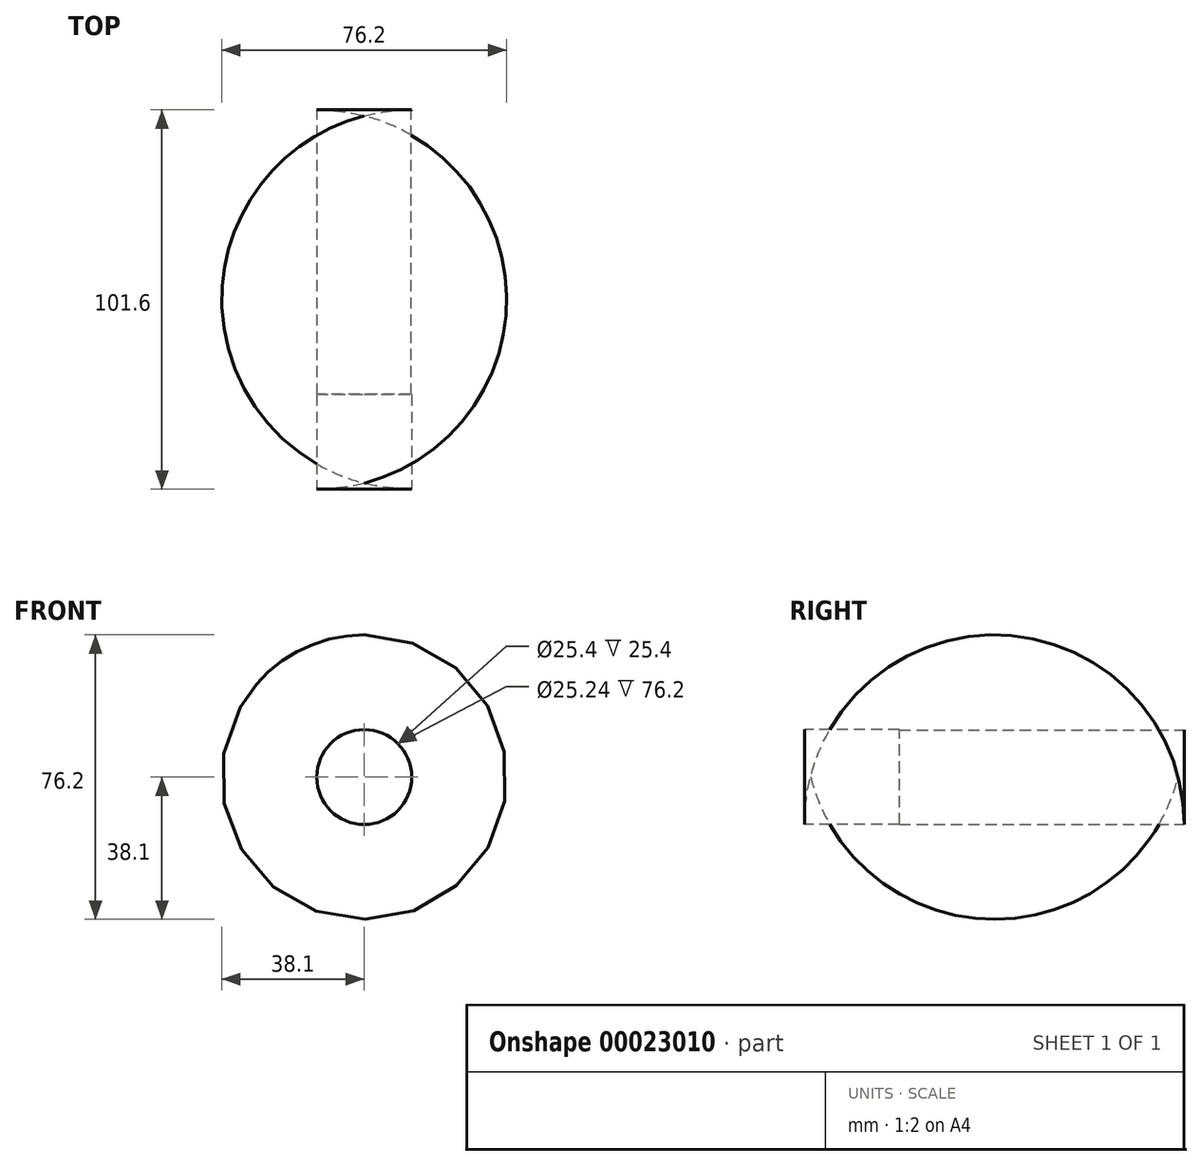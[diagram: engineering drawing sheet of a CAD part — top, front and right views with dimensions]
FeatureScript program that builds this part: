
annotation { "Feature Type Name" : "Feature", "Feature Type Description" : "" }
export const myFeature = defineFeature(function(context is Context, id is Id, definition is map)
    precondition{}
    {
        {
            var Q0;
            Q0=qCreatedBy(makeId("Front.planeOp"),FACE);
            var sketch = newSketch(context, id + "F0", { "sketchPlane" : qUnion([Q0])});
            skCircle(sketch, "E0", {"center": v(0, 0) * mm, "radius": 63.5 * mm});
            skSolve(sketch);
        }
        {
            var Q0;
            Q0=makeQuery(id+"F0.imprint","IMPRINT",FACE,{"disambiguationData":[TD([[makeQuery(id+"F0.imprint","IMPRINT",EDGE,{"derivedFrom":sQuery(id+"F0.wireOp",EDGE,"E0")}),1.0]])]});
            extrude(context, id + "F1", {"entities" : qUnion([Q0]), "depth" : 101.6 * mm});
        }
        {
            var Q0;
            Q0=makeQuery(id+"F1.opExtrude","CAP_EDGE",EDGE,{"disambiguationData":[OSD([sQuery(id+"F0.wireOp",EDGE,"E0")])],"isStart":false});
            var Q1;
            Q1=makeQuery(id+"F1.opExtrude","CAP_EDGE",EDGE,{"disambiguationData":[OSD([sQuery(id+"F0.wireOp",EDGE,"E0")])],"isStart":true});
            fillet(context, id + "F2", {"entities" : qUnion([Q0, Q1]), "radius" : 50.8 * mm, "tangentPropagation" : true, "allowEdgeOverflow" : false});
        }
        {
            var Q0;
            Q0=qCreatedBy(makeId("Front.planeOp"),FACE);
            var sketch = newSketch(context, id + "F3", { "sketchPlane" : qUnion([Q0])});
            skCircle(sketch, "E1", {"center": v(0, 0) * mm, "radius": 12.62 * mm});
            skSolve(sketch);
        }
        {
            var Q0;
            Q0=qCreatedBy(makeId("Front.planeOp"),FACE);
            var sketch = newSketch(context, id + "F4", { "sketchPlane" : qUnion([Q0])});
            skCircle(sketch, "E2", {"center": v(0, 0) * mm, "radius": 12.35 * mm});
            skSolve(sketch);
        }
        {
            var Q0;
            Q0 = qSketchRegion(id + "F4", true);
            extrude(context, id + "F5", {"entities" : qUnion([Q0]), "operationType" : NewBodyOperationType.REMOVE, "oppositeDirection" : true, "depth" : 101.6 * mm});
        }
        {
            var Q0;
            Q0=makeQuery(id+"F1.opExtrude","CAP_FACE",FACE,{"disambiguationData":[OSD([sQuery(id+"F0.wireOp",EDGE,"E0")])],"isStart":false});
            extrude(context, id + "F6", {"entities" : qUnion([Q0]), "operationType" : NewBodyOperationType.REMOVE, "oppositeDirection" : true, "depth" : 25.4 * mm});
        }
        {
            var Q0;
            Q0=makeQuery(id+"F3.imprint","IMPRINT",FACE,{"disambiguationData":[TD([[makeQuery(id+"F3.imprint","IMPRINT",EDGE,{"derivedFrom":sQuery(id+"F3.wireOp",EDGE,"E1")}),1.0]])]});
            extrude(context, id + "F7", {"entities" : qUnion([Q0]), "operationType" : NewBodyOperationType.REMOVE, "depth" : 101.6 * mm});
        }
    });
